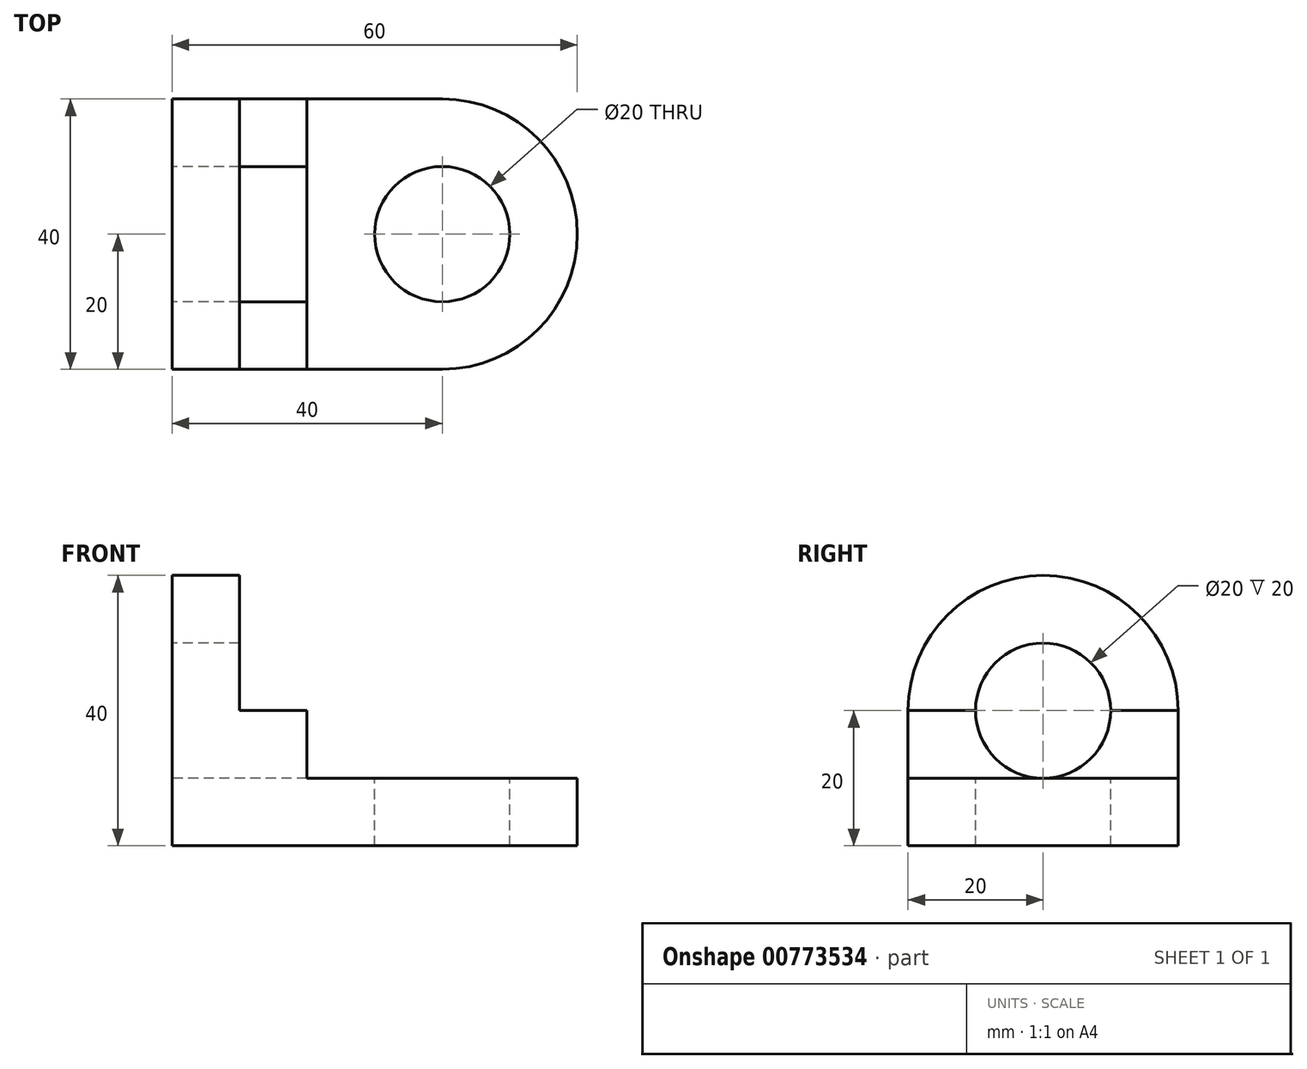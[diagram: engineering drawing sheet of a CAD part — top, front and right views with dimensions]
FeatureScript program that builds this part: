
annotation { "Feature Type Name" : "Feature", "Feature Type Description" : "" }
export const myFeature = defineFeature(function(context is Context, id is Id, definition is map)
    precondition{}
    {
        {
            var Q0;
            Q0=qCreatedBy(makeId("Top.planeOp"),FACE);
            var sketch = newSketch(context, id + "F0", { "sketchPlane" : qUnion([Q0])});
            skLineSegment(sketch, "E0.bottom", {"start": v(20, 20) * mm, "end": v(-20, 20) * mm});
            skLineSegment(sketch, "E0.top", {"start": v(20, -20) * mm, "end": v(-20, -20) * mm});
            skLineSegment(sketch, "E0.left", {"start": v(20, 20) * mm, "end": v(20, -20) * mm});
            skLineSegment(sketch, "E0.right", {"start": v(-20, 20) * mm, "end": v(-20, -20) * mm});
            skPoint(sketch, "E0.middle", {"position": v(0, 0) * mm});
            skSolve(sketch);
        }
        {
            var Q0;
            Q0=makeQuery(id+"F0.imprint","IMPRINT",FACE,{"disambiguationData":[TD([[makeQuery(id+"F0.imprint","IMPRINT",EDGE,{"derivedFrom":sQuery(id+"F0.wireOp",EDGE,"E0.bottom")}),1.0]])]});
            extrude(context, id + "F1", {"entities" : qUnion([Q0]), "depth" : 10 * mm, "offsetDistance" : 25 * mm});
        }
        {
            var Q0;
            Q0=makeQuery(id+"F1.opExtrude","CAP_FACE",FACE,{"disambiguationData":[OSD([sQuery(id+"F0.wireOp",EDGE,"E0.bottom"),sQuery(id+"F0.wireOp",EDGE,"E0.top"),sQuery(id+"F0.wireOp",EDGE,"E0.left"),sQuery(id+"F0.wireOp",EDGE,"E0.right")])],"isStart":true});
            var sketch = newSketch(context, id + "F2", { "sketchPlane" : qUnion([Q0])});
            skArc(sketch, "E1", {"start": v(20, -20) * mm, "mid": v(40, 0) * mm, "end": v(20, 20) * mm});
            skSolve(sketch);
        }
        {
            var Q0;
            Q0=makeQuery(id+"F2.imprint","IMPRINT",FACE,{"disambiguationData":[TD([[makeQuery(id+"F2.imprint","IMPRINT",EDGE,{"derivedFrom":sQuery(id+"F2.wireOp",EDGE,"E1")}),1.0]])]});
            extrude(context, id + "F3", {"entities" : qUnion([Q0]), "operationType" : NewBodyOperationType.ADD, "oppositeDirection" : true, "depth" : 10 * mm, "offsetDistance" : 25 * mm});
        }
        {
            var Q0;
            {var subQ0=sQuery(id+"F0.wireOp",EDGE,"E0.left");Q0=makeQuery(id+"F3.boolean.opBoolean","MERGE",FACE,{"derivedFrom":[makeQuery(id+"F1.opExtrude","CAP_FACE",FACE,{"disambiguationData":[OSD([sQuery(id+"F0.wireOp",EDGE,"E0.bottom"),sQuery(id+"F0.wireOp",EDGE,"E0.top"),subQ0,sQuery(id+"F0.wireOp",EDGE,"E0.right")])],"isStart":false}),makeQuery(id+"F3.opExtrude","CAP_FACE",FACE,{"disambiguationData":[OSD([subQ0,sQuery(id+"F2.wireOp",EDGE,"E1")])],"isStart":false})]});}
            var sketch = newSketch(context, id + "F4", { "sketchPlane" : qUnion([Q0])});
            skCircle(sketch, "E2", {"center": v(20, 0) * mm, "radius": 10 * mm});
            skSolve(sketch);
        }
        {
            var Q0;
            Q0=makeQuery(id+"F4.imprint","IMPRINT",FACE,{"disambiguationData":[TD([[makeQuery(id+"F4.imprint","IMPRINT",EDGE,{"derivedFrom":sQuery(id+"F4.wireOp",EDGE,"E2")}),1.0]])]});
            extrude(context, id + "F5", {"entities" : qUnion([Q0]), "operationType" : NewBodyOperationType.REMOVE, "oppositeDirection" : true, "depth" : 10 * mm, "offsetDistance" : 25 * mm});
        }
        {
            var Q0;
            {var subQ0=sQuery(id+"F0.wireOp",EDGE,"E0.left");Q0=makeQuery(id+"F3.boolean.opBoolean","MERGE",FACE,{"derivedFrom":[makeQuery(id+"F1.opExtrude","CAP_FACE",FACE,{"disambiguationData":[OSD([sQuery(id+"F0.wireOp",EDGE,"E0.bottom"),sQuery(id+"F0.wireOp",EDGE,"E0.top"),subQ0,sQuery(id+"F0.wireOp",EDGE,"E0.right")])],"isStart":false}),makeQuery(id+"F3.opExtrude","CAP_FACE",FACE,{"disambiguationData":[OSD([subQ0,sQuery(id+"F2.wireOp",EDGE,"E1")])],"isStart":false})]});}
            var sketch = newSketch(context, id + "F6", { "sketchPlane" : qUnion([Q0])});
            skLineSegment(sketch, "E3.bottom", {"start": v(-20, 20) * mm, "end": v(0, 20) * mm});
            skLineSegment(sketch, "E3.top", {"start": v(-20, -20) * mm, "end": v(0, -20) * mm});
            skLineSegment(sketch, "E3.left", {"start": v(-20, 20) * mm, "end": v(-20, -20) * mm});
            skLineSegment(sketch, "E3.right", {"start": v(0, 20) * mm, "end": v(0, -20) * mm});
            skSolve(sketch);
        }
        {
            var Q0;
            Q0=makeQuery(id+"F6.imprint","IMPRINT",FACE,{"disambiguationData":[TD([[makeQuery(id+"F6.imprint","IMPRINT",EDGE,{"derivedFrom":sQuery(id+"F6.wireOp",EDGE,"E3.bottom")}),1.0]])]});
            extrude(context, id + "F7", {"entities" : qUnion([Q0]), "operationType" : NewBodyOperationType.ADD, "depth" : 10 * mm, "offsetDistance" : 25 * mm});
        }
        {
            var Q0;
            Q0=makeQuery(id+"F7.boolean.opBoolean","MERGE",FACE,{"derivedFrom":[makeQuery(id+"F1.opExtrude","SWEPT_FACE",FACE,{"disambiguationData":[OSD([sQuery(id+"F0.wireOp",EDGE,"E0.right")])]}),makeQuery(id+"F7.opExtrude","SWEPT_FACE",FACE,{"disambiguationData":[OSD([sQuery(id+"F6.wireOp",EDGE,"E3.left")])]})]});
            var sketch = newSketch(context, id + "F8", { "sketchPlane" : qUnion([Q0])});
            skArc(sketch, "E4", {"start": v(20, 20) * mm, "mid": v(0, 40) * mm, "end": v(-20, 20) * mm});
            skSolve(sketch);
        }
        {
            var Q0;
            Q0=makeQuery(id+"F8.imprint","IMPRINT",FACE,{"disambiguationData":[TD([[makeQuery(id+"F8.imprint","IMPRINT",EDGE,{"derivedFrom":sQuery(id+"F8.wireOp",EDGE,"E4")}),1.0]])]});
            extrude(context, id + "F9", {"entities" : qUnion([Q0]), "operationType" : NewBodyOperationType.ADD, "oppositeDirection" : true, "depth" : 10 * mm, "offsetDistance" : 25 * mm});
        }
        {
            var Q0;
            {var subQ0=sQuery(id+"F6.wireOp",EDGE,"E3.left");Q0=makeQuery(id+"F9.boolean.opBoolean","MERGE",FACE,{"derivedFrom":[makeQuery(id+"F7.boolean.opBoolean","MERGE",FACE,{"derivedFrom":[makeQuery(id+"F1.opExtrude","SWEPT_FACE",FACE,{"disambiguationData":[OSD([sQuery(id+"F0.wireOp",EDGE,"E0.right")])]}),makeQuery(id+"F7.opExtrude","SWEPT_FACE",FACE,{"disambiguationData":[OSD([subQ0])]})]}),makeQuery(id+"F9.opExtrude","CAP_FACE",FACE,{"disambiguationData":[OSD([subQ0,sQuery(id+"F8.wireOp",EDGE,"E4")])],"isStart":true})]});}
            var sketch = newSketch(context, id + "F10", { "sketchPlane" : qUnion([Q0])});
            skCircle(sketch, "E5", {"center": v(0, 20) * mm, "radius": 10 * mm});
            skSolve(sketch);
        }
        {
            var Q0;
            Q0=makeQuery(id+"F10.imprint","IMPRINT",FACE,{"disambiguationData":[TD([[makeQuery(id+"F10.imprint","IMPRINT",EDGE,{"derivedFrom":sQuery(id+"F10.wireOp",EDGE,"E5")}),1.0]])]});
            extrude(context, id + "F11", {"entities" : qUnion([Q0]), "operationType" : NewBodyOperationType.REMOVE, "oppositeDirection" : true, "depth" : 20 * mm, "offsetDistance" : 25 * mm});
        }
    });
